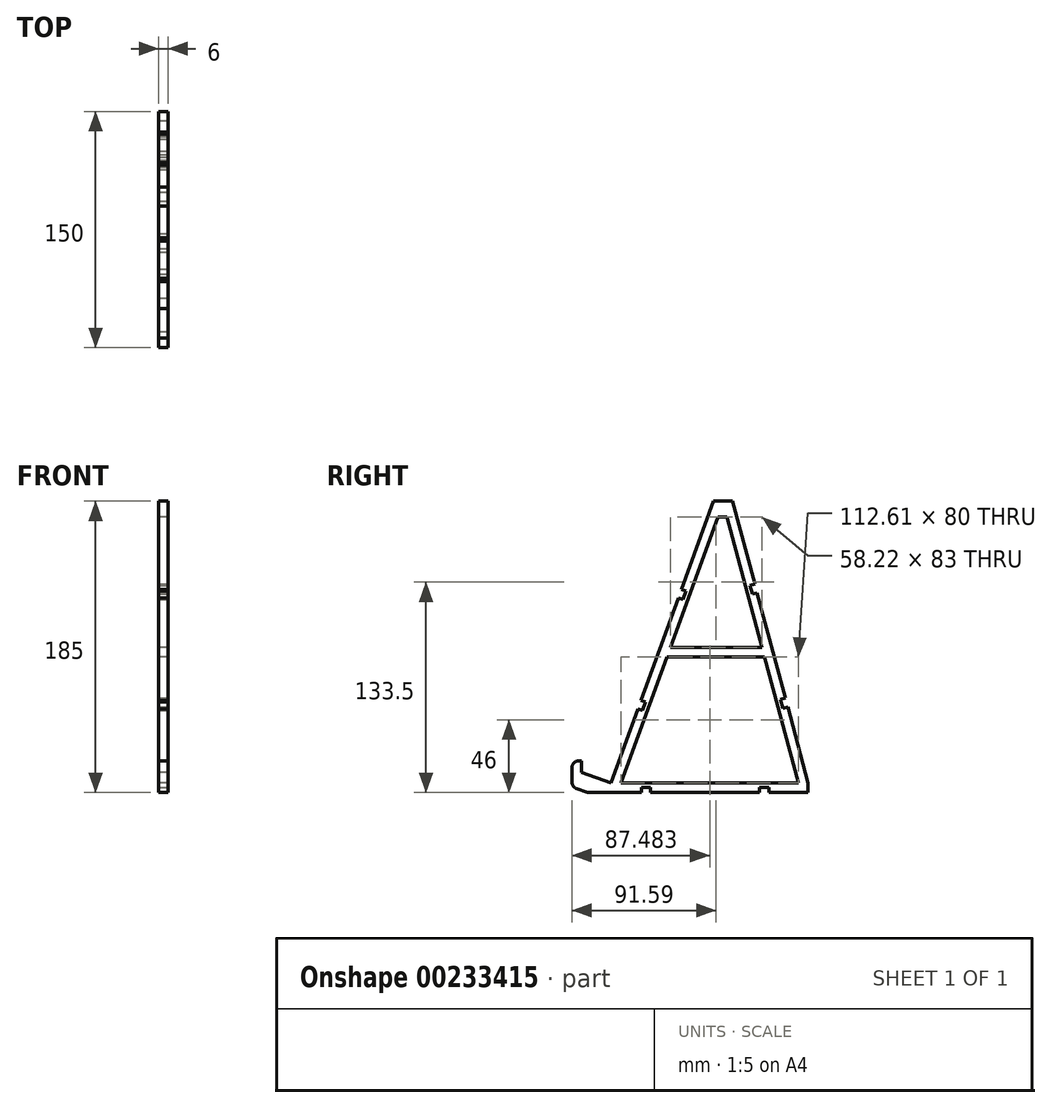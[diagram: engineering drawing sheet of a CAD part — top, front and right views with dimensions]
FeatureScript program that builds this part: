
annotation { "Feature Type Name" : "Feature", "Feature Type Description" : "" }
export const myFeature = defineFeature(function(context is Context, id is Id, definition is map)
    precondition{}
    {
        {
            var Q0;
            Q0=qCreatedBy(makeId("Right.planeOp"),FACE);
            var sketch = newSketch(context, id + "F0", { "sketchPlane" : qUnion([Q0])});
            skLineSegment(sketch, "E0", {"start": v(-65, 0) * mm, "end": v(75, 0) * mm});
            skLineSegment(sketch, "E1", {"start": v(-75, 3.64) * mm, "end": v(-75, 20) * mm});
            skLineSegment(sketch, "E2", {"start": v(-50.2, 6) * mm, "end": v(14.94, 185) * mm});
            skLineSegment(sketch, "E3", {"start": v(14.94, 185) * mm, "end": v(26.94, 185) * mm});
            skLineSegment(sketch, "E4", {"start": v(26.94, 185) * mm, "end": v(75, 6) * mm});
            skLineSegment(sketch, "E5", {"start": v(75, 6) * mm, "end": v(75, 0) * mm});
            skLineSegment(sketch, "E6", {"start": v(-43.82, 6) * mm, "end": v(-14.7, 86) * mm});
            skLineSegment(sketch, "E7", {"start": v(17.69, 175) * mm, "end": v(23.42, 175) * mm});
            skLineSegment(sketch, "E8", {"start": v(23.42, 175) * mm, "end": v(45.7, 92) * mm});
            skLineSegment(sketch, "E9", {"start": v(68.79, 6) * mm, "end": v(-43.82, 6) * mm});
            skLineSegment(sketch, "E10", {"start": v(-12.52, 92) * mm, "end": v(45.7, 92) * mm});
            skLineSegment(sketch, "E11", {"start": v(-14.7, 86) * mm, "end": v(47.31, 86) * mm});
            skLineSegment(sketch, "E12.trimOffspring", {"start": v(-12.52, 92) * mm, "end": v(17.69, 175) * mm});
            skLineSegment(sketch, "E13.trimOffspring", {"start": v(47.31, 86) * mm, "end": v(68.79, 6) * mm});
            skLineSegment(sketch, "E14", {"start": v(-50.2, 6) * mm, "end": v(-69, 12.84) * mm});
            skLineSegment(sketch, "E15", {"start": v(-69, 12.84) * mm, "end": v(-69, 20) * mm});
            skLineSegment(sketch, "E16", {"start": v(-75, 20) * mm, "end": v(-69, 20) * mm});
            skLineSegment(sketch, "E17", {"start": v(-75, 3.64) * mm, "end": v(-65, 0) * mm});
            skPoint(sketch, "E18.orphan", {"position": v(-75, 0) * mm});
            skSolve(sketch);
        }
        {
            var Q0;
            Q0=qSketchRegion(id+"F0",true);
            extrude(context, id + "F1", {"entities" : qUnion([Q0]), "depth" : 6 * mm});
        }
        {
            var Q0;
            Q0=makeQuery(id+"F1.opExtrude","CAP_FACE",FACE,{"disambiguationData":[OSD([sQuery(id+"F0.wireOp",EDGE,"E0"),sQuery(id+"F0.wireOp",EDGE,"E1"),sQuery(id+"F0.wireOp",EDGE,"E2"),sQuery(id+"F0.wireOp",EDGE,"E3"),sQuery(id+"F0.wireOp",EDGE,"E4"),sQuery(id+"F0.wireOp",EDGE,"E5"),sQuery(id+"F0.wireOp",EDGE,"E6"),sQuery(id+"F0.wireOp",EDGE,"E7"),sQuery(id+"F0.wireOp",EDGE,"E8"),sQuery(id+"F0.wireOp",EDGE,"E9"),sQuery(id+"F0.wireOp",EDGE,"E10"),sQuery(id+"F0.wireOp",EDGE,"E11"),sQuery(id+"F0.wireOp",EDGE,"E12.trimOffspring"),sQuery(id+"F0.wireOp",EDGE,"E13.trimOffspring"),sQuery(id+"F0.wireOp",EDGE,"E14"),sQuery(id+"F0.wireOp",EDGE,"E15"),sQuery(id+"F0.wireOp",EDGE,"E16"),sQuery(id+"F0.wireOp",EDGE,"E17")])],"isStart":false});
            var sketch = newSketch(context, id + "F2", { "sketchPlane" : qUnion([Q0])});
            skLineSegment(sketch, "E19.bottom", {"start": v(-30.8, 0) * mm, "end": v(-25, 0) * mm});
            skLineSegment(sketch, "E19.top", {"start": v(-30.8, 3.1) * mm, "end": v(-25, 3.1) * mm});
            skLineSegment(sketch, "E19.left", {"start": v(-30.8, 0) * mm, "end": v(-30.8, 3.1) * mm});
            skLineSegment(sketch, "E19.right", {"start": v(-25, 0) * mm, "end": v(-25, 3.1) * mm});
            skPoint(sketch, "E20.oppositeSnap0", {"position": v(-27.9, 3.1) * mm});
            skLineSegment(sketch, "E20.bottom", {"start": v(44.2, 0) * mm, "end": v(50, 0) * mm});
            skLineSegment(sketch, "E20.top", {"start": v(44.2, 3.1) * mm, "end": v(50, 3.1) * mm});
            skLineSegment(sketch, "E20.left", {"start": v(44.2, 0) * mm, "end": v(44.2, 3.1) * mm});
            skLineSegment(sketch, "E20.right", {"start": v(50, 0) * mm, "end": v(50, 3.1) * mm});
            skLineSegment(sketch, "E21.bottom", {"start": v(-31.12, 58.43) * mm, "end": v(-28.2, 57.37) * mm});
            skLineSegment(sketch, "E21.top", {"start": v(-33.1, 52.98) * mm, "end": v(-30.2, 51.92) * mm});
            skLineSegment(sketch, "E21.left", {"start": v(-31.12, 58.43) * mm, "end": v(-33.1, 52.98) * mm});
            skLineSegment(sketch, "E21.right", {"start": v(-28.2, 57.37) * mm, "end": v(-30.2, 51.92) * mm});
            skLineSegment(sketch, "E22.bottom", {"start": v(-5.47, 128.91) * mm, "end": v(-2.56, 127.85) * mm});
            skLineSegment(sketch, "E22.top", {"start": v(-7.45, 123.46) * mm, "end": v(-4.54, 122.4) * mm});
            skLineSegment(sketch, "E22.left", {"start": v(-5.47, 128.91) * mm, "end": v(-7.45, 123.46) * mm});
            skLineSegment(sketch, "E22.right", {"start": v(-2.56, 127.85) * mm, "end": v(-4.54, 122.4) * mm});
            skLineSegment(sketch, "E23.bottom", {"start": v(57.54, 59.09) * mm, "end": v(60.53, 59.9) * mm});
            skLineSegment(sketch, "E23.top", {"start": v(59.04, 53.49) * mm, "end": v(62.04, 54.3) * mm});
            skLineSegment(sketch, "E23.left", {"start": v(57.54, 59.09) * mm, "end": v(59.04, 53.49) * mm});
            skLineSegment(sketch, "E23.right", {"start": v(60.53, 59.9) * mm, "end": v(62.04, 54.3) * mm});
            skLineSegment(sketch, "E24.bottom", {"start": v(38.1, 131.52) * mm, "end": v(41.09, 132.33) * mm});
            skLineSegment(sketch, "E24.top", {"start": v(39.6, 125.92) * mm, "end": v(42.59, 126.73) * mm});
            skLineSegment(sketch, "E24.left", {"start": v(38.1, 131.52) * mm, "end": v(39.6, 125.92) * mm});
            skLineSegment(sketch, "E24.right", {"start": v(41.09, 132.33) * mm, "end": v(42.59, 126.73) * mm});
            skSolve(sketch);
        }
        {
            var Q0;
            Q0=makeQuery(id+"F2.imprint","IMPRINT",FACE,{"disambiguationData":[TD([[makeQuery(id+"F2.imprint","IMPRINT",EDGE,{"derivedFrom":sQuery(id+"F2.wireOp",EDGE,"E19.bottom")}),1.0]])]});
            var Q1;
            Q1=makeQuery(id+"F2.imprint","IMPRINT",FACE,{"disambiguationData":[TD([[makeQuery(id+"F2.imprint","IMPRINT",EDGE,{"derivedFrom":sQuery(id+"F2.wireOp",EDGE,"E20.bottom")}),1.0]])]});
            var Q2;
            Q2=makeQuery(id+"F2.imprint","IMPRINT",FACE,{"disambiguationData":[TD([[makeQuery(id+"F2.imprint","IMPRINT",EDGE,{"derivedFrom":sQuery(id+"F2.wireOp",EDGE,"E22.bottom")}),-1.0]])]});
            var Q3;
            Q3=makeQuery(id+"F2.imprint","IMPRINT",FACE,{"disambiguationData":[TD([[makeQuery(id+"F2.imprint","IMPRINT",EDGE,{"derivedFrom":sQuery(id+"F2.wireOp",EDGE,"E21.bottom")}),-1.0]])]});
            var Q4;
            Q4=makeQuery(id+"F2.imprint","IMPRINT",FACE,{"disambiguationData":[TD([[makeQuery(id+"F2.imprint","IMPRINT",EDGE,{"derivedFrom":sQuery(id+"F2.wireOp",EDGE,"E23.bottom")}),-1.0]])]});
            var Q5;
            Q5=makeQuery(id+"F2.imprint","IMPRINT",FACE,{"disambiguationData":[TD([[makeQuery(id+"F2.imprint","IMPRINT",EDGE,{"derivedFrom":sQuery(id+"F2.wireOp",EDGE,"E24.bottom")}),-1.0]])]});
            extrude(context, id + "F3", {"entities" : qUnion([Q0, Q1, Q2, Q3, Q4, Q5]), "operationType" : NewBodyOperationType.REMOVE, "oppositeDirection" : true, "depth" : 25 * mm});
        }
        {
            var Q0;
            Q0=makeQuery(id+"F3.boolean.opBoolean","COPY",FACE,{"derivedFrom":makeQuery(id+"F3.opExtrude","SWEPT_FACE",FACE,{"disambiguationData":[OSD([sQuery(id+"F2.wireOp",EDGE,"E21.top")])]})});
            var sketch = newSketch(context, id + "F4", { "sketchPlane" : qUnion([Q0])});
            skCircle(sketch, "E25", {"center": v(3, -46.13) * mm, "radius": 0.75 * mm});
            skSolve(sketch);
        }
        {
            var Q0;
            {var subQ0=sQuery(id+"F4.wireOp",EDGE,"E25");var subQ1=makeQuery(id+"F3.boolean.opBoolean","COPY",EDGE,{"derivedFrom":makeQuery(id+"F3.opExtrude","SWEPT_EDGE",EDGE,{"disambiguationData":[OSD([sQuery(id+"F2.wireOp",EDGE,"E21.top"),sQuery(id+"F2.wireOp",EDGE,"E21.right")])]})});var subQ2=makeQuery(id+"F4.imprint","INTERSECT",VERTEX,{"disambiguationData":[OD(0.0)],"derivedFrom":[subQ1,subQ0]});Q0=makeQuery(id+"F4.imprint","IMPRINT",FACE,{"disambiguationData":[TD([[makeQuery(id+"F4.imprint","IMPRINT",EDGE,{"disambiguationData":[TD([[subQ2,1.0]])],"derivedFrom":subQ0}),1.0]])]});}
            var Q1;
            Q1=makeQuery(id+"F3.boolean.opBoolean","COPY",FACE,{"derivedFrom":makeQuery(id+"F3.opExtrude","SWEPT_FACE",FACE,{"disambiguationData":[OSD([sQuery(id+"F2.wireOp",EDGE,"E22.bottom")])]})});
            extrude(context, id + "F5", {"entities" : qUnion([Q0]), "operationType" : NewBodyOperationType.ADD, "endBound" : BoundingType.UP_TO_SURFACE, "endBoundEntityFace" : qUnion([Q1]), "depth" : 25 * mm});
        }
        {
            var Q0;
            Q0=makeQuery(id+"F3.boolean.opBoolean","COPY",FACE,{"derivedFrom":makeQuery(id+"F3.opExtrude","SWEPT_FACE",FACE,{"disambiguationData":[OSD([sQuery(id+"F2.wireOp",EDGE,"E19.left")])]})});
            var sketch = newSketch(context, id + "F6", { "sketchPlane" : qUnion([Q0])});
            skCircle(sketch, "E26", {"center": v(-3, 3.1) * mm, "radius": 0.75 * mm});
            skSolve(sketch);
        }
        {
            var Q0;
            {var subQ0=sQuery(id+"F6.wireOp",EDGE,"E26");var subQ1=makeQuery(id+"F3.boolean.opBoolean","COPY",EDGE,{"derivedFrom":makeQuery(id+"F3.opExtrude","SWEPT_EDGE",EDGE,{"disambiguationData":[OSD([sQuery(id+"F2.wireOp",EDGE,"E19.top"),sQuery(id+"F2.wireOp",EDGE,"E19.left")])]})});var subQ2=makeQuery(id+"F6.imprint","INTERSECT",VERTEX,{"disambiguationData":[OD(0.0)],"derivedFrom":[subQ1,subQ0]});Q0=makeQuery(id+"F6.imprint","IMPRINT",FACE,{"disambiguationData":[TD([[makeQuery(id+"F6.imprint","IMPRINT",EDGE,{"disambiguationData":[TD([[subQ2,-1.0]])],"derivedFrom":subQ0}),1.0]])]});}
            var Q1;
            Q1=makeQuery(id+"F3.boolean.opBoolean","COPY",FACE,{"derivedFrom":makeQuery(id+"F3.opExtrude","SWEPT_FACE",FACE,{"disambiguationData":[OSD([sQuery(id+"F2.wireOp",EDGE,"E20.right")])]})});
            extrude(context, id + "F7", {"entities" : qUnion([Q0]), "operationType" : NewBodyOperationType.ADD, "endBound" : BoundingType.UP_TO_SURFACE, "endBoundEntityFace" : qUnion([Q1]), "depth" : 25 * mm});
        }
        {
            var Q0;
            Q0=makeQuery(id+"F3.boolean.opBoolean","COPY",FACE,{"derivedFrom":makeQuery(id+"F3.opExtrude","SWEPT_FACE",FACE,{"disambiguationData":[OSD([sQuery(id+"F2.wireOp",EDGE,"E23.top")])]})});
            var sketch = newSketch(context, id + "F8", { "sketchPlane" : qUnion([Q0])});
            skCircle(sketch, "E27", {"center": v(3, 70.9) * mm, "radius": 0.75 * mm});
            skSolve(sketch);
        }
        {
            var Q0;
            {var subQ0=sQuery(id+"F8.wireOp",EDGE,"E27");var subQ1=makeQuery(id+"F3.boolean.opBoolean","COPY",EDGE,{"derivedFrom":makeQuery(id+"F3.opExtrude","SWEPT_EDGE",EDGE,{"disambiguationData":[OSD([sQuery(id+"F2.wireOp",EDGE,"E23.top"),sQuery(id+"F2.wireOp",EDGE,"E23.left")])]})});var subQ2=makeQuery(id+"F8.imprint","INTERSECT",VERTEX,{"disambiguationData":[OD(0.0)],"derivedFrom":[subQ1,subQ0]});Q0=makeQuery(id+"F8.imprint","IMPRINT",FACE,{"disambiguationData":[TD([[makeQuery(id+"F8.imprint","IMPRINT",EDGE,{"disambiguationData":[TD([[subQ2,-1.0]])],"derivedFrom":subQ0}),1.0]])]});}
            var Q1;
            Q1=makeQuery(id+"F3.boolean.opBoolean","COPY",FACE,{"derivedFrom":makeQuery(id+"F3.opExtrude","SWEPT_FACE",FACE,{"disambiguationData":[OSD([sQuery(id+"F2.wireOp",EDGE,"E24.bottom")])]})});
            extrude(context, id + "F9", {"entities" : qUnion([Q0]), "operationType" : NewBodyOperationType.ADD, "endBound" : BoundingType.UP_TO_SURFACE, "endBoundEntityFace" : qUnion([Q1]), "depth" : 25 * mm});
        }
        {
            var Q0;
            Q0=makeQuery(id+"F1.opExtrude","SWEPT_EDGE",EDGE,{"disambiguationData":[OSD([sQuery(id+"F0.wireOp",EDGE,"E1"),sQuery(id+"F0.wireOp",EDGE,"E17")])]});
            var Q1;
            Q1=makeQuery(id+"F1.opExtrude","SWEPT_EDGE",EDGE,{"disambiguationData":[OSD([sQuery(id+"F0.wireOp",EDGE,"E1"),sQuery(id+"F0.wireOp",EDGE,"E16")])]});
            fillet(context, id + "F10", {"entities" : qUnion([Q0, Q1]), "radius" : 4 * mm, "tangentPropagation" : true, "allowEdgeOverflow" : false});
        }
    });
